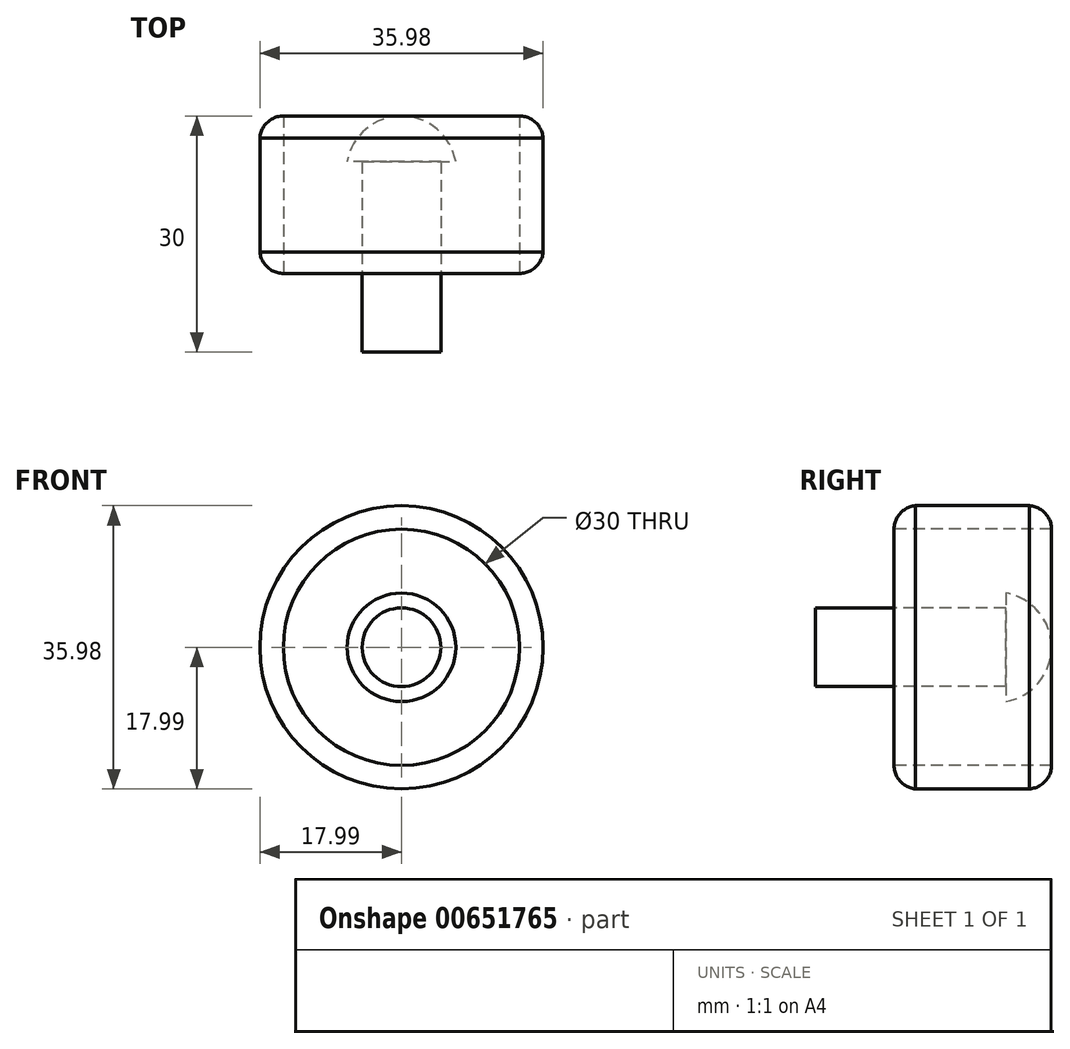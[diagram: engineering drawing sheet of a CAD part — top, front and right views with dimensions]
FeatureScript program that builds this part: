
annotation { "Feature Type Name" : "Feature", "Feature Type Description" : "" }
export const myFeature = defineFeature(function(context is Context, id is Id, definition is map)
    precondition{}
    {
        {
            var Q0;
            Q0=qCreatedBy(makeId("Right.planeOp"),FACE);
            var sketch = newSketch(context, id + "F0", { "sketchPlane" : qUnion([Q0])});
            skPoint(sketch, "E0.end.orphan", {"position": v(0, 70.3) * mm});
            skPoint(sketch, "E1.end.orphan", {"position": v(0, 55.13) * mm});
            skPoint(sketch, "E2.end.orphan", {"position": v(19.32, 0) * mm});
            skPoint(sketch, "E3.start.orphan", {"position": v(19.32, 2.32) * mm});
            skPoint(sketch, "E4.center.orphan", {"position": v(16.69, 2.32) * mm});
            skPoint(sketch, "E4.start.orphan", {"position": v(35.37, 0) * mm});
            skPoint(sketch, "E5.end.orphan", {"position": v(0, 10.46) * mm});
            skArc(sketch, "E6", {"start": v(15, 0) * mm, "mid": v(13.35, 4.51) * mm, "end": v(9.18, 6.9) * mm});
            skLineSegment(sketch, "E7", {"start": v(9.18, 6.9) * mm, "end": v(9.18, 5) * mm});
            skLineSegment(sketch, "E8", {"start": v(9.18, 5) * mm, "end": v(0, 5) * mm});
            skLineSegment(sketch, "E9", {"start": v(0, 10.46) * mm, "end": v(0, 5) * mm, "construction": true});
            skLineSegment(sketch, "E10", {"start": v(0, 0) * mm, "end": v(15, 0) * mm});
            skPoint(sketch, "E11.start.orphan", {"position": v(-6.18, 62.03) * mm});
            skPoint(sketch, "E12.end.orphan", {"position": v(9.36, 62.03) * mm});
            skLineSegment(sketch, "E13", {"start": v(0, 5) * mm, "end": v(-15, 5) * mm});
            skLineSegment(sketch, "E14", {"start": v(-15, 5) * mm, "end": v(-15, 0) * mm});
            skLineSegment(sketch, "E15", {"start": v(-15, 0) * mm, "end": v(0, 0) * mm});
            skPoint(sketch, "E16.end.orphan", {"position": v(13.85, 0) * mm});
            skLineSegment(sketch, "E17", {"start": v(15, 0) * mm, "end": v(15, 15) * mm});
            skLineSegment(sketch, "E18", {"start": v(15, 15) * mm, "end": v(-5, 15) * mm});
            skLineSegment(sketch, "E19", {"start": v(-2.26, 17.99) * mm, "end": v(12.18, 17.99) * mm});
            skArc(sketch, "E20", {"start": v(15, 15) * mm, "mid": v(14.18, 17.05) * mm, "end": v(12.18, 17.99) * mm});
            skArc(sketch, "E21", {"start": v(-2.26, 17.99) * mm, "mid": v(-4.21, 17.03) * mm, "end": v(-5, 15) * mm});
            skSolve(sketch);
        }
        {
            var Q0;
            Q0=makeQuery(id+"F0.imprint","IMPRINT",FACE,{"disambiguationData":[TD([[makeQuery(id+"F0.imprint","IMPRINT",EDGE,{"derivedFrom":sQuery(id+"F0.wireOp",EDGE,"E18")}),-1.0]])]});
            var Q1;
            Q1=makeQuery(id+"F0.imprint","IMPRINT",FACE,{"disambiguationData":[TD([[makeQuery(id+"F0.imprint","IMPRINT",EDGE,{"derivedFrom":sQuery(id+"F0.wireOp",EDGE,"E6")}),1.0]])]});
            var Q2;
            Q2=sQuery(id+"F0.wireOp",EDGE,"E15");
            revolve(context, id + "F1", {"surfaceOperationType" : NewSurfaceOperationType.NEW, "entities" : qUnion([Q0, Q1]), "axis" : qUnion([Q2]), "revolveType" : RevolveType.FULL});
        }
    });
